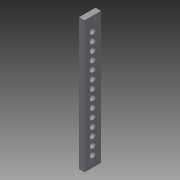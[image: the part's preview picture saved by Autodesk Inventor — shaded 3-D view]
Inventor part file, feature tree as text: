
AUTODESK INVENTOR PART (.ipt)
format: ipt  version: 2014 SP1 (Build 180222100, 222)  size: 94,720 bytes
history: native  units: in
note: dims shown in document units (in); Inventor stores cm internally (conversion verified against a paired STEP export)
features: extrude x1, sketch x1
ambient origin geometry x8: Origin, YZ Plane, XZ Plane, XY Plane, X Axis, Y Axis, Z Axis, Center Point
bodies: Solid1 (feature_tree)
feature tree (2):
  extrude  "Extrusion1"  Depth=6.0in
  sketch  "Sketch1"  dims[d0=0.75in d1=6.0in d2=0.25in d3=0.5in d4=0.375in d5=5.5118in d7=0.375in d8=0.3937in d10=1.0in d12=0.25in d13=0.0in]
